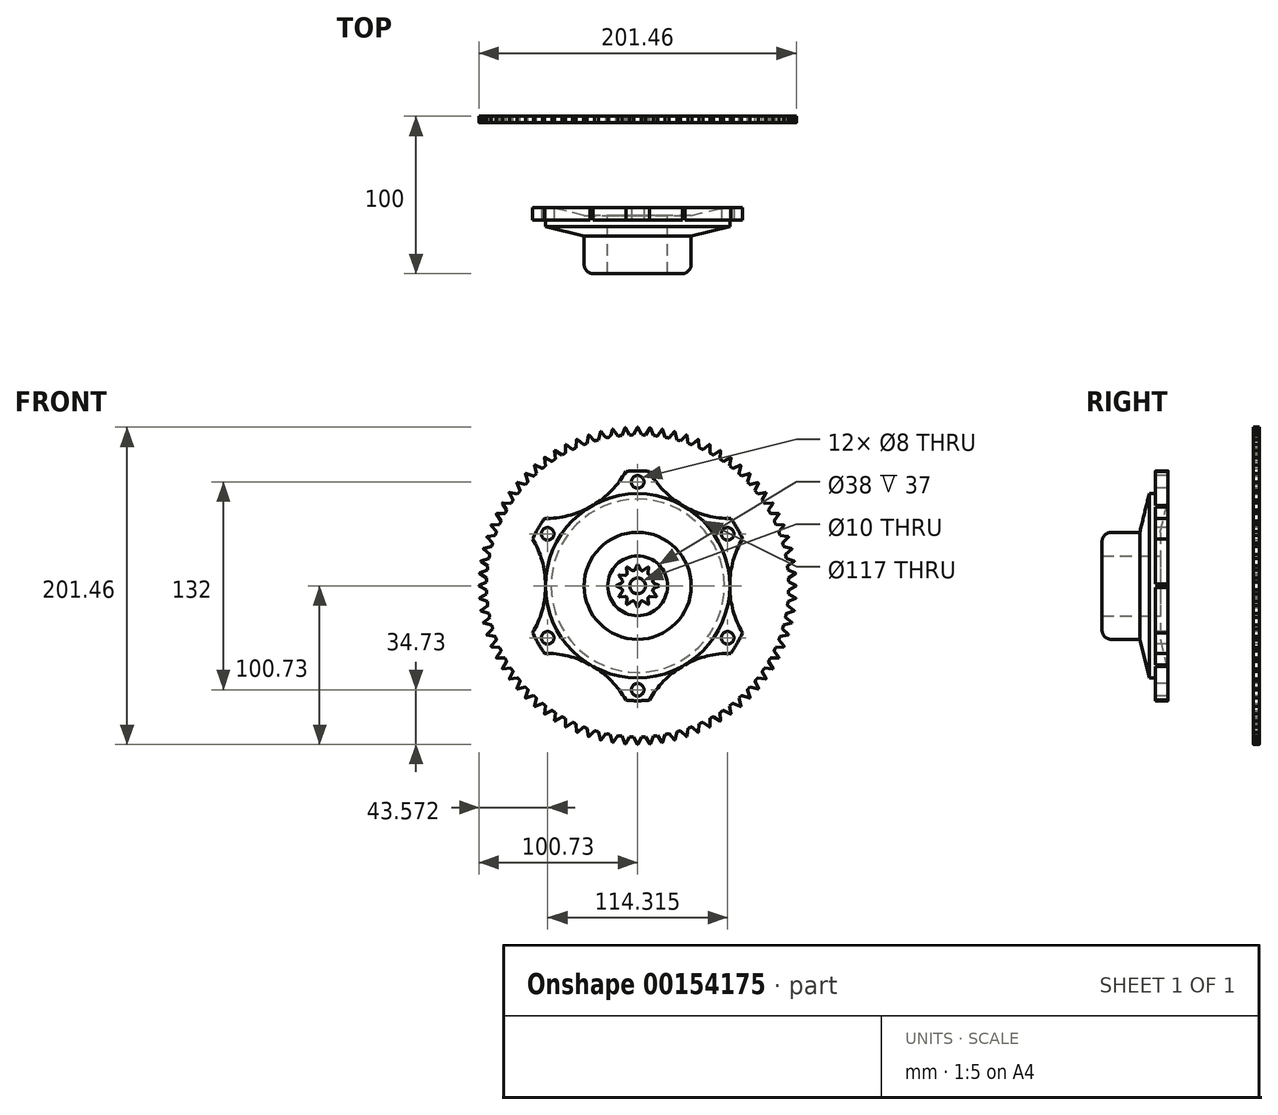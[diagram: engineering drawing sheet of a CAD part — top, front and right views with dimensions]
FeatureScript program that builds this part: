
annotation { "Feature Type Name" : "Feature", "Feature Type Description" : "" }
export const myFeature = defineFeature(function(context is Context, id is Id, definition is map)
    precondition{}
    {
        {
            var Q0;
            Q0=qCreatedBy(makeId("Front.planeOp"),FACE);
            var sketch = newSketch(context, id + "F0", { "sketchPlane" : qUnion([Q0])});
            skCircle(sketch, "E0", {"center": v(0, 0) * mm, "radius": 58.5 * mm});
            skCircle(sketch, "E1", {"center": v(0, 0) * mm, "radius": 96 * mm});
            skPoint(sketch, "E2", {"position": v(0, 101) * mm});
            skPoint(sketch, "E3", {"position": v(0, 96) * mm});
            skPoint(sketch, "E4", {"position": v(-2.5, 95.97) * mm});
            skPoint(sketch, "E5", {"position": v(2.5, 95.97) * mm});
            skLineSegment(sketch, "E6", {"start": v(-0.2, 100.6) * mm, "end": v(-2.5, 95.97) * mm});
            skLineSegment(sketch, "E7", {"start": v(0.2, 100.6) * mm, "end": v(2.5, 95.97) * mm});
            skArc(sketch, "E8.filletArc", {"start": v(0.2, 100.6) * mm, "mid": v(0, 100.73) * mm, "end": v(-0.2, 100.6) * mm});
            skLineSegment(sketch, "E9.1.0", {"start": v(-8.09, 100.28) * mm, "end": v(-10.02, 95.48) * mm});
            skLineSegment(sketch, "E9.1.1", {"start": v(-7.7, 100.3) * mm, "end": v(-5.04, 95.87) * mm});
            skArc(sketch, "E9.1.2", {"start": v(-7.7, 100.3) * mm, "mid": v(-7.9, 100.42) * mm, "end": v(-8.09, 100.28) * mm});
            skLineSegment(sketch, "E9.2.0", {"start": v(-15.93, 99.33) * mm, "end": v(-17.48, 94.4) * mm});
            skLineSegment(sketch, "E9.2.1", {"start": v(-15.54, 99.4) * mm, "end": v(-12.54, 95.18) * mm});
            skArc(sketch, "E9.2.2", {"start": v(-15.54, 99.4) * mm, "mid": v(-15.76, 99.49) * mm, "end": v(-15.93, 99.33) * mm});
            skLineSegment(sketch, "E9.3.0", {"start": v(-23.68, 97.78) * mm, "end": v(-24.83, 92.73) * mm});
            skLineSegment(sketch, "E9.3.1", {"start": v(-23.3, 97.87) * mm, "end": v(-19.97, 93.9) * mm});
            skArc(sketch, "E9.3.2", {"start": v(-23.3, 97.87) * mm, "mid": v(-23.51, 97.94) * mm, "end": v(-23.68, 97.78) * mm});
            skLineSegment(sketch, "E9.4.0", {"start": v(-31.28, 95.62) * mm, "end": v(-32.03, 90.5) * mm});
            skLineSegment(sketch, "E9.4.1", {"start": v(-30.9, 95.74) * mm, "end": v(-27.28, 92.04) * mm});
            skArc(sketch, "E9.4.2", {"start": v(-30.9, 95.74) * mm, "mid": v(-31.13, 95.8) * mm, "end": v(-31.28, 95.62) * mm});
            skLineSegment(sketch, "E9.5.0", {"start": v(-38.68, 92.87) * mm, "end": v(-39.03, 87.7) * mm});
            skLineSegment(sketch, "E9.5.1", {"start": v(-38.32, 93.02) * mm, "end": v(-34.42, 89.62) * mm});
            skArc(sketch, "E9.5.2", {"start": v(-38.32, 93.02) * mm, "mid": v(-38.55, 93.06) * mm, "end": v(-38.68, 92.87) * mm});
            skLineSegment(sketch, "E9.6.0", {"start": v(-45.85, 89.55) * mm, "end": v(-45.8, 84.37) * mm});
            skLineSegment(sketch, "E9.6.1", {"start": v(-45.5, 89.73) * mm, "end": v(-41.34, 86.64) * mm});
            skArc(sketch, "E9.6.2", {"start": v(-45.5, 89.73) * mm, "mid": v(-45.73, 89.75) * mm, "end": v(-45.85, 89.55) * mm});
            skLineSegment(sketch, "E9.7.0", {"start": v(-52.73, 85.68) * mm, "end": v(-52.27, 80.52) * mm});
            skLineSegment(sketch, "E9.7.1", {"start": v(-52.4, 85.88) * mm, "end": v(-48.01, 83.13) * mm});
            skArc(sketch, "E9.7.2", {"start": v(-52.4, 85.88) * mm, "mid": v(-52.63, 85.88) * mm, "end": v(-52.73, 85.68) * mm});
            skLineSegment(sketch, "E9.8.0", {"start": v(-59.3, 81.27) * mm, "end": v(-58.43, 76.17) * mm});
            skLineSegment(sketch, "E9.8.1", {"start": v(-58.97, 81.5) * mm, "end": v(-54.39, 79.1) * mm});
            skArc(sketch, "E9.8.2", {"start": v(-58.97, 81.5) * mm, "mid": v(-59.2, 81.49) * mm, "end": v(-59.3, 81.27) * mm});
            skLineSegment(sketch, "E9.9.0", {"start": v(-65.49, 76.37) * mm, "end": v(-64.23, 71.35) * mm});
            skLineSegment(sketch, "E9.9.1", {"start": v(-65.19, 76.63) * mm, "end": v(-60.42, 74.6) * mm});
            skArc(sketch, "E9.9.2", {"start": v(-65.19, 76.63) * mm, "mid": v(-65.42, 76.6) * mm, "end": v(-65.49, 76.37) * mm});
            skLineSegment(sketch, "E9.10.0", {"start": v(-71.28, 71) * mm, "end": v(-69.63, 66.1) * mm});
            skLineSegment(sketch, "E9.10.1", {"start": v(-71, 71.28) * mm, "end": v(-66.1, 69.63) * mm});
            skArc(sketch, "E9.10.2", {"start": v(-71, 71.28) * mm, "mid": v(-71.22, 71.22) * mm, "end": v(-71.28, 71) * mm});
            skLineSegment(sketch, "E9.11.0", {"start": v(-76.63, 65.19) * mm, "end": v(-74.6, 60.43) * mm});
            skLineSegment(sketch, "E9.11.1", {"start": v(-76.37, 65.49) * mm, "end": v(-71.35, 64.23) * mm});
            skArc(sketch, "E9.11.2", {"start": v(-76.37, 65.49) * mm, "mid": v(-76.6, 65.42) * mm, "end": v(-76.63, 65.19) * mm});
            skLineSegment(sketch, "E9.12.0", {"start": v(-81.5, 58.97) * mm, "end": v(-79.1, 54.39) * mm});
            skLineSegment(sketch, "E9.12.1", {"start": v(-81.27, 59.3) * mm, "end": v(-76.17, 58.43) * mm});
            skArc(sketch, "E9.12.2", {"start": v(-81.27, 59.3) * mm, "mid": v(-81.49, 59.2) * mm, "end": v(-81.5, 58.97) * mm});
            skLineSegment(sketch, "E9.13.0", {"start": v(-85.88, 52.4) * mm, "end": v(-83.13, 48.01) * mm});
            skLineSegment(sketch, "E9.13.1", {"start": v(-85.68, 52.73) * mm, "end": v(-80.52, 52.27) * mm});
            skArc(sketch, "E9.13.2", {"start": v(-85.68, 52.73) * mm, "mid": v(-85.88, 52.63) * mm, "end": v(-85.88, 52.4) * mm});
            skLineSegment(sketch, "E9.14.0", {"start": v(-89.73, 45.5) * mm, "end": v(-86.64, 41.34) * mm});
            skLineSegment(sketch, "E9.14.1", {"start": v(-89.55, 45.85) * mm, "end": v(-84.37, 45.8) * mm});
            skArc(sketch, "E9.14.2", {"start": v(-89.55, 45.85) * mm, "mid": v(-89.75, 45.73) * mm, "end": v(-89.73, 45.5) * mm});
            skLineSegment(sketch, "E9.15.0", {"start": v(-93.02, 38.32) * mm, "end": v(-89.62, 34.42) * mm});
            skLineSegment(sketch, "E9.15.1", {"start": v(-92.87, 38.68) * mm, "end": v(-87.7, 39.03) * mm});
            skArc(sketch, "E9.15.2", {"start": v(-92.87, 38.68) * mm, "mid": v(-93.06, 38.55) * mm, "end": v(-93.02, 38.32) * mm});
            skLineSegment(sketch, "E9.16.0", {"start": v(-95.74, 30.9) * mm, "end": v(-92.04, 27.28) * mm});
            skLineSegment(sketch, "E9.16.1", {"start": v(-95.62, 31.28) * mm, "end": v(-90.5, 32.03) * mm});
            skArc(sketch, "E9.16.2", {"start": v(-95.62, 31.28) * mm, "mid": v(-95.8, 31.13) * mm, "end": v(-95.74, 30.9) * mm});
            skLineSegment(sketch, "E9.17.0", {"start": v(-97.87, 23.3) * mm, "end": v(-93.9, 19.97) * mm});
            skLineSegment(sketch, "E9.17.1", {"start": v(-97.78, 23.68) * mm, "end": v(-92.73, 24.83) * mm});
            skArc(sketch, "E9.17.2", {"start": v(-97.78, 23.68) * mm, "mid": v(-97.94, 23.51) * mm, "end": v(-97.87, 23.3) * mm});
            skLineSegment(sketch, "E9.18.0", {"start": v(-99.4, 15.54) * mm, "end": v(-95.18, 12.54) * mm});
            skLineSegment(sketch, "E9.18.1", {"start": v(-99.33, 15.93) * mm, "end": v(-94.4, 17.48) * mm});
            skArc(sketch, "E9.18.2", {"start": v(-99.33, 15.93) * mm, "mid": v(-99.49, 15.76) * mm, "end": v(-99.4, 15.54) * mm});
            skLineSegment(sketch, "E9.19.0", {"start": v(-100.3, 7.7) * mm, "end": v(-95.87, 5.04) * mm});
            skLineSegment(sketch, "E9.19.1", {"start": v(-100.28, 8.09) * mm, "end": v(-95.48, 10.02) * mm});
            skArc(sketch, "E9.19.2", {"start": v(-100.28, 8.09) * mm, "mid": v(-100.42, 7.9) * mm, "end": v(-100.3, 7.7) * mm});
            skLineSegment(sketch, "E9.20.0", {"start": v(-100.6, -0.2) * mm, "end": v(-95.97, -2.5) * mm});
            skLineSegment(sketch, "E9.20.1", {"start": v(-100.6, 0.2) * mm, "end": v(-95.97, 2.5) * mm});
            skArc(sketch, "E9.20.2", {"start": v(-100.6, 0.2) * mm, "mid": v(-100.73, 0) * mm, "end": v(-100.6, -0.2) * mm});
            skLineSegment(sketch, "E9.21.0", {"start": v(-100.28, -8.09) * mm, "end": v(-95.48, -10.02) * mm});
            skLineSegment(sketch, "E9.21.1", {"start": v(-100.3, -7.7) * mm, "end": v(-95.87, -5.04) * mm});
            skArc(sketch, "E9.21.2", {"start": v(-100.3, -7.7) * mm, "mid": v(-100.42, -7.9) * mm, "end": v(-100.28, -8.09) * mm});
            skLineSegment(sketch, "E9.22.0", {"start": v(-99.33, -15.93) * mm, "end": v(-94.4, -17.48) * mm});
            skLineSegment(sketch, "E9.22.1", {"start": v(-99.4, -15.54) * mm, "end": v(-95.18, -12.54) * mm});
            skArc(sketch, "E9.22.2", {"start": v(-99.4, -15.54) * mm, "mid": v(-99.49, -15.76) * mm, "end": v(-99.33, -15.93) * mm});
            skLineSegment(sketch, "E9.23.0", {"start": v(-97.78, -23.68) * mm, "end": v(-92.73, -24.83) * mm});
            skLineSegment(sketch, "E9.23.1", {"start": v(-97.87, -23.3) * mm, "end": v(-93.9, -19.97) * mm});
            skArc(sketch, "E9.23.2", {"start": v(-97.87, -23.3) * mm, "mid": v(-97.94, -23.51) * mm, "end": v(-97.78, -23.68) * mm});
            skLineSegment(sketch, "E9.24.0", {"start": v(-95.62, -31.28) * mm, "end": v(-90.5, -32.03) * mm});
            skLineSegment(sketch, "E9.24.1", {"start": v(-95.74, -30.9) * mm, "end": v(-92.04, -27.28) * mm});
            skArc(sketch, "E9.24.2", {"start": v(-95.74, -30.9) * mm, "mid": v(-95.8, -31.13) * mm, "end": v(-95.62, -31.28) * mm});
            skLineSegment(sketch, "E9.25.0", {"start": v(-92.87, -38.68) * mm, "end": v(-87.7, -39.03) * mm});
            skLineSegment(sketch, "E9.25.1", {"start": v(-93.02, -38.32) * mm, "end": v(-89.62, -34.42) * mm});
            skArc(sketch, "E9.25.2", {"start": v(-93.02, -38.32) * mm, "mid": v(-93.06, -38.55) * mm, "end": v(-92.87, -38.68) * mm});
            skLineSegment(sketch, "E9.26.0", {"start": v(-89.55, -45.85) * mm, "end": v(-84.37, -45.8) * mm});
            skLineSegment(sketch, "E9.26.1", {"start": v(-89.73, -45.5) * mm, "end": v(-86.64, -41.34) * mm});
            skArc(sketch, "E9.26.2", {"start": v(-89.73, -45.5) * mm, "mid": v(-89.75, -45.73) * mm, "end": v(-89.55, -45.85) * mm});
            skLineSegment(sketch, "E9.27.0", {"start": v(-85.68, -52.73) * mm, "end": v(-80.52, -52.27) * mm});
            skLineSegment(sketch, "E9.27.1", {"start": v(-85.88, -52.4) * mm, "end": v(-83.13, -48.01) * mm});
            skArc(sketch, "E9.27.2", {"start": v(-85.88, -52.4) * mm, "mid": v(-85.88, -52.63) * mm, "end": v(-85.68, -52.73) * mm});
            skLineSegment(sketch, "E9.28.0", {"start": v(-81.27, -59.3) * mm, "end": v(-76.17, -58.43) * mm});
            skLineSegment(sketch, "E9.28.1", {"start": v(-81.5, -58.97) * mm, "end": v(-79.1, -54.39) * mm});
            skArc(sketch, "E9.28.2", {"start": v(-81.5, -58.97) * mm, "mid": v(-81.49, -59.2) * mm, "end": v(-81.27, -59.3) * mm});
            skLineSegment(sketch, "E9.29.0", {"start": v(-76.37, -65.49) * mm, "end": v(-71.35, -64.23) * mm});
            skLineSegment(sketch, "E9.29.1", {"start": v(-76.63, -65.19) * mm, "end": v(-74.6, -60.42) * mm});
            skArc(sketch, "E9.29.2", {"start": v(-76.63, -65.19) * mm, "mid": v(-76.6, -65.42) * mm, "end": v(-76.37, -65.49) * mm});
            skLineSegment(sketch, "E9.30.0", {"start": v(-71, -71.28) * mm, "end": v(-66.1, -69.63) * mm});
            skLineSegment(sketch, "E9.30.1", {"start": v(-71.28, -71) * mm, "end": v(-69.63, -66.1) * mm});
            skArc(sketch, "E9.30.2", {"start": v(-71.28, -71) * mm, "mid": v(-71.22, -71.22) * mm, "end": v(-71, -71.28) * mm});
            skLineSegment(sketch, "E9.31.0", {"start": v(-65.19, -76.63) * mm, "end": v(-60.43, -74.6) * mm});
            skLineSegment(sketch, "E9.31.1", {"start": v(-65.49, -76.37) * mm, "end": v(-64.23, -71.35) * mm});
            skArc(sketch, "E9.31.2", {"start": v(-65.49, -76.37) * mm, "mid": v(-65.42, -76.6) * mm, "end": v(-65.19, -76.63) * mm});
            skLineSegment(sketch, "E9.32.0", {"start": v(-58.97, -81.5) * mm, "end": v(-54.39, -79.1) * mm});
            skLineSegment(sketch, "E9.32.1", {"start": v(-59.3, -81.27) * mm, "end": v(-58.43, -76.17) * mm});
            skArc(sketch, "E9.32.2", {"start": v(-59.3, -81.27) * mm, "mid": v(-59.2, -81.49) * mm, "end": v(-58.97, -81.5) * mm});
            skLineSegment(sketch, "E9.33.0", {"start": v(-52.4, -85.88) * mm, "end": v(-48.01, -83.13) * mm});
            skLineSegment(sketch, "E9.33.1", {"start": v(-52.73, -85.68) * mm, "end": v(-52.27, -80.52) * mm});
            skArc(sketch, "E9.33.2", {"start": v(-52.73, -85.68) * mm, "mid": v(-52.63, -85.88) * mm, "end": v(-52.4, -85.88) * mm});
            skLineSegment(sketch, "E9.34.0", {"start": v(-45.5, -89.73) * mm, "end": v(-41.34, -86.64) * mm});
            skLineSegment(sketch, "E9.34.1", {"start": v(-45.85, -89.55) * mm, "end": v(-45.8, -84.37) * mm});
            skArc(sketch, "E9.34.2", {"start": v(-45.85, -89.55) * mm, "mid": v(-45.73, -89.75) * mm, "end": v(-45.5, -89.73) * mm});
            skLineSegment(sketch, "E9.35.0", {"start": v(-38.32, -93.02) * mm, "end": v(-34.42, -89.62) * mm});
            skLineSegment(sketch, "E9.35.1", {"start": v(-38.68, -92.87) * mm, "end": v(-39.03, -87.7) * mm});
            skArc(sketch, "E9.35.2", {"start": v(-38.68, -92.87) * mm, "mid": v(-38.55, -93.06) * mm, "end": v(-38.32, -93.02) * mm});
            skLineSegment(sketch, "E9.36.0", {"start": v(-30.9, -95.74) * mm, "end": v(-27.28, -92.04) * mm});
            skLineSegment(sketch, "E9.36.1", {"start": v(-31.28, -95.62) * mm, "end": v(-32.03, -90.5) * mm});
            skArc(sketch, "E9.36.2", {"start": v(-31.28, -95.62) * mm, "mid": v(-31.13, -95.8) * mm, "end": v(-30.9, -95.74) * mm});
            skLineSegment(sketch, "E9.37.0", {"start": v(-23.3, -97.87) * mm, "end": v(-19.97, -93.9) * mm});
            skLineSegment(sketch, "E9.37.1", {"start": v(-23.68, -97.78) * mm, "end": v(-24.83, -92.73) * mm});
            skArc(sketch, "E9.37.2", {"start": v(-23.68, -97.78) * mm, "mid": v(-23.51, -97.94) * mm, "end": v(-23.3, -97.87) * mm});
            skLineSegment(sketch, "E9.38.0", {"start": v(-15.54, -99.4) * mm, "end": v(-12.54, -95.18) * mm});
            skLineSegment(sketch, "E9.38.1", {"start": v(-15.93, -99.33) * mm, "end": v(-17.48, -94.4) * mm});
            skArc(sketch, "E9.38.2", {"start": v(-15.93, -99.33) * mm, "mid": v(-15.76, -99.49) * mm, "end": v(-15.54, -99.4) * mm});
            skLineSegment(sketch, "E9.39.0", {"start": v(-7.7, -100.3) * mm, "end": v(-5.04, -95.87) * mm});
            skLineSegment(sketch, "E9.39.1", {"start": v(-8.09, -100.28) * mm, "end": v(-10.02, -95.48) * mm});
            skArc(sketch, "E9.39.2", {"start": v(-8.09, -100.28) * mm, "mid": v(-7.9, -100.42) * mm, "end": v(-7.7, -100.3) * mm});
            skLineSegment(sketch, "E9.40.0", {"start": v(0.2, -100.6) * mm, "end": v(2.5, -95.97) * mm});
            skLineSegment(sketch, "E9.40.1", {"start": v(-0.2, -100.6) * mm, "end": v(-2.5, -95.97) * mm});
            skArc(sketch, "E9.40.2", {"start": v(-0.2, -100.6) * mm, "mid": v(0, -100.73) * mm, "end": v(0.2, -100.6) * mm});
            skLineSegment(sketch, "E9.41.0", {"start": v(8.09, -100.28) * mm, "end": v(10.02, -95.48) * mm});
            skLineSegment(sketch, "E9.41.1", {"start": v(7.7, -100.3) * mm, "end": v(5.04, -95.87) * mm});
            skArc(sketch, "E9.41.2", {"start": v(7.7, -100.3) * mm, "mid": v(7.9, -100.42) * mm, "end": v(8.09, -100.28) * mm});
            skLineSegment(sketch, "E9.42.0", {"start": v(15.93, -99.33) * mm, "end": v(17.48, -94.4) * mm});
            skLineSegment(sketch, "E9.42.1", {"start": v(15.54, -99.4) * mm, "end": v(12.54, -95.18) * mm});
            skArc(sketch, "E9.42.2", {"start": v(15.54, -99.4) * mm, "mid": v(15.76, -99.49) * mm, "end": v(15.93, -99.33) * mm});
            skLineSegment(sketch, "E9.43.0", {"start": v(23.68, -97.78) * mm, "end": v(24.83, -92.73) * mm});
            skLineSegment(sketch, "E9.43.1", {"start": v(23.3, -97.87) * mm, "end": v(19.97, -93.9) * mm});
            skArc(sketch, "E9.43.2", {"start": v(23.3, -97.87) * mm, "mid": v(23.51, -97.94) * mm, "end": v(23.68, -97.78) * mm});
            skLineSegment(sketch, "E9.44.0", {"start": v(31.28, -95.62) * mm, "end": v(32.03, -90.5) * mm});
            skLineSegment(sketch, "E9.44.1", {"start": v(30.9, -95.74) * mm, "end": v(27.28, -92.04) * mm});
            skArc(sketch, "E9.44.2", {"start": v(30.9, -95.74) * mm, "mid": v(31.13, -95.8) * mm, "end": v(31.28, -95.62) * mm});
            skLineSegment(sketch, "E9.45.0", {"start": v(38.68, -92.87) * mm, "end": v(39.03, -87.7) * mm});
            skLineSegment(sketch, "E9.45.1", {"start": v(38.32, -93.02) * mm, "end": v(34.42, -89.62) * mm});
            skArc(sketch, "E9.45.2", {"start": v(38.32, -93.02) * mm, "mid": v(38.55, -93.06) * mm, "end": v(38.68, -92.87) * mm});
            skLineSegment(sketch, "E9.46.0", {"start": v(45.85, -89.55) * mm, "end": v(45.8, -84.37) * mm});
            skLineSegment(sketch, "E9.46.1", {"start": v(45.5, -89.73) * mm, "end": v(41.34, -86.64) * mm});
            skArc(sketch, "E9.46.2", {"start": v(45.5, -89.73) * mm, "mid": v(45.73, -89.75) * mm, "end": v(45.85, -89.55) * mm});
            skLineSegment(sketch, "E9.47.0", {"start": v(52.73, -85.68) * mm, "end": v(52.27, -80.52) * mm});
            skLineSegment(sketch, "E9.47.1", {"start": v(52.4, -85.88) * mm, "end": v(48.01, -83.13) * mm});
            skArc(sketch, "E9.47.2", {"start": v(52.4, -85.88) * mm, "mid": v(52.63, -85.88) * mm, "end": v(52.73, -85.68) * mm});
            skLineSegment(sketch, "E9.48.0", {"start": v(59.3, -81.27) * mm, "end": v(58.43, -76.17) * mm});
            skLineSegment(sketch, "E9.48.1", {"start": v(58.97, -81.5) * mm, "end": v(54.39, -79.1) * mm});
            skArc(sketch, "E9.48.2", {"start": v(58.97, -81.5) * mm, "mid": v(59.2, -81.49) * mm, "end": v(59.3, -81.27) * mm});
            skLineSegment(sketch, "E9.49.0", {"start": v(65.49, -76.37) * mm, "end": v(64.23, -71.35) * mm});
            skLineSegment(sketch, "E9.49.1", {"start": v(65.19, -76.63) * mm, "end": v(60.42, -74.6) * mm});
            skArc(sketch, "E9.49.2", {"start": v(65.19, -76.63) * mm, "mid": v(65.42, -76.6) * mm, "end": v(65.49, -76.37) * mm});
            skLineSegment(sketch, "E9.50.0", {"start": v(71.28, -71) * mm, "end": v(69.63, -66.1) * mm});
            skLineSegment(sketch, "E9.50.1", {"start": v(71, -71.28) * mm, "end": v(66.1, -69.63) * mm});
            skArc(sketch, "E9.50.2", {"start": v(71, -71.28) * mm, "mid": v(71.22, -71.22) * mm, "end": v(71.28, -71) * mm});
            skLineSegment(sketch, "E9.51.0", {"start": v(76.63, -65.19) * mm, "end": v(74.6, -60.43) * mm});
            skLineSegment(sketch, "E9.51.1", {"start": v(76.37, -65.49) * mm, "end": v(71.35, -64.23) * mm});
            skArc(sketch, "E9.51.2", {"start": v(76.37, -65.49) * mm, "mid": v(76.6, -65.42) * mm, "end": v(76.63, -65.19) * mm});
            skLineSegment(sketch, "E9.52.0", {"start": v(81.5, -58.97) * mm, "end": v(79.1, -54.39) * mm});
            skLineSegment(sketch, "E9.52.1", {"start": v(81.27, -59.3) * mm, "end": v(76.17, -58.43) * mm});
            skArc(sketch, "E9.52.2", {"start": v(81.27, -59.3) * mm, "mid": v(81.49, -59.2) * mm, "end": v(81.5, -58.97) * mm});
            skLineSegment(sketch, "E9.53.0", {"start": v(85.88, -52.4) * mm, "end": v(83.13, -48.01) * mm});
            skLineSegment(sketch, "E9.53.1", {"start": v(85.68, -52.73) * mm, "end": v(80.52, -52.27) * mm});
            skArc(sketch, "E9.53.2", {"start": v(85.68, -52.73) * mm, "mid": v(85.88, -52.63) * mm, "end": v(85.88, -52.4) * mm});
            skLineSegment(sketch, "E9.54.0", {"start": v(89.73, -45.5) * mm, "end": v(86.64, -41.34) * mm});
            skLineSegment(sketch, "E9.54.1", {"start": v(89.55, -45.85) * mm, "end": v(84.37, -45.8) * mm});
            skArc(sketch, "E9.54.2", {"start": v(89.55, -45.85) * mm, "mid": v(89.75, -45.73) * mm, "end": v(89.73, -45.5) * mm});
            skLineSegment(sketch, "E9.55.0", {"start": v(93.02, -38.32) * mm, "end": v(89.62, -34.42) * mm});
            skLineSegment(sketch, "E9.55.1", {"start": v(92.87, -38.68) * mm, "end": v(87.7, -39.03) * mm});
            skArc(sketch, "E9.55.2", {"start": v(92.87, -38.68) * mm, "mid": v(93.06, -38.55) * mm, "end": v(93.02, -38.32) * mm});
            skLineSegment(sketch, "E9.56.0", {"start": v(95.74, -30.9) * mm, "end": v(92.04, -27.28) * mm});
            skLineSegment(sketch, "E9.56.1", {"start": v(95.62, -31.28) * mm, "end": v(90.5, -32.03) * mm});
            skArc(sketch, "E9.56.2", {"start": v(95.62, -31.28) * mm, "mid": v(95.8, -31.13) * mm, "end": v(95.74, -30.9) * mm});
            skLineSegment(sketch, "E9.57.0", {"start": v(97.87, -23.3) * mm, "end": v(93.9, -19.97) * mm});
            skLineSegment(sketch, "E9.57.1", {"start": v(97.78, -23.68) * mm, "end": v(92.73, -24.83) * mm});
            skArc(sketch, "E9.57.2", {"start": v(97.78, -23.68) * mm, "mid": v(97.94, -23.51) * mm, "end": v(97.87, -23.3) * mm});
            skLineSegment(sketch, "E9.58.0", {"start": v(99.4, -15.54) * mm, "end": v(95.18, -12.54) * mm});
            skLineSegment(sketch, "E9.58.1", {"start": v(99.33, -15.93) * mm, "end": v(94.4, -17.48) * mm});
            skArc(sketch, "E9.58.2", {"start": v(99.33, -15.93) * mm, "mid": v(99.49, -15.76) * mm, "end": v(99.4, -15.54) * mm});
            skLineSegment(sketch, "E9.59.0", {"start": v(100.3, -7.7) * mm, "end": v(95.87, -5.04) * mm});
            skLineSegment(sketch, "E9.59.1", {"start": v(100.28, -8.09) * mm, "end": v(95.48, -10.02) * mm});
            skArc(sketch, "E9.59.2", {"start": v(100.28, -8.09) * mm, "mid": v(100.42, -7.9) * mm, "end": v(100.3, -7.7) * mm});
            skLineSegment(sketch, "E9.60.0", {"start": v(100.6, 0.2) * mm, "end": v(95.97, 2.5) * mm});
            skLineSegment(sketch, "E9.60.1", {"start": v(100.6, -0.2) * mm, "end": v(95.97, -2.5) * mm});
            skArc(sketch, "E9.60.2", {"start": v(100.6, -0.2) * mm, "mid": v(100.73, 0) * mm, "end": v(100.6, 0.2) * mm});
            skLineSegment(sketch, "E9.61.0", {"start": v(100.28, 8.09) * mm, "end": v(95.48, 10.02) * mm});
            skLineSegment(sketch, "E9.61.1", {"start": v(100.3, 7.7) * mm, "end": v(95.87, 5.04) * mm});
            skArc(sketch, "E9.61.2", {"start": v(100.3, 7.7) * mm, "mid": v(100.42, 7.9) * mm, "end": v(100.28, 8.09) * mm});
            skLineSegment(sketch, "E9.62.0", {"start": v(99.33, 15.93) * mm, "end": v(94.4, 17.48) * mm});
            skLineSegment(sketch, "E9.62.1", {"start": v(99.4, 15.54) * mm, "end": v(95.18, 12.54) * mm});
            skArc(sketch, "E9.62.2", {"start": v(99.4, 15.54) * mm, "mid": v(99.49, 15.76) * mm, "end": v(99.33, 15.93) * mm});
            skLineSegment(sketch, "E9.63.0", {"start": v(97.78, 23.68) * mm, "end": v(92.73, 24.83) * mm});
            skLineSegment(sketch, "E9.63.1", {"start": v(97.87, 23.3) * mm, "end": v(93.9, 19.97) * mm});
            skArc(sketch, "E9.63.2", {"start": v(97.87, 23.3) * mm, "mid": v(97.94, 23.51) * mm, "end": v(97.78, 23.68) * mm});
            skLineSegment(sketch, "E9.64.0", {"start": v(95.62, 31.28) * mm, "end": v(90.5, 32.03) * mm});
            skLineSegment(sketch, "E9.64.1", {"start": v(95.74, 30.9) * mm, "end": v(92.04, 27.28) * mm});
            skArc(sketch, "E9.64.2", {"start": v(95.74, 30.9) * mm, "mid": v(95.8, 31.13) * mm, "end": v(95.62, 31.28) * mm});
            skLineSegment(sketch, "E9.65.0", {"start": v(92.87, 38.68) * mm, "end": v(87.7, 39.03) * mm});
            skLineSegment(sketch, "E9.65.1", {"start": v(93.02, 38.32) * mm, "end": v(89.62, 34.42) * mm});
            skArc(sketch, "E9.65.2", {"start": v(93.02, 38.32) * mm, "mid": v(93.06, 38.55) * mm, "end": v(92.87, 38.68) * mm});
            skLineSegment(sketch, "E9.66.0", {"start": v(89.55, 45.85) * mm, "end": v(84.37, 45.8) * mm});
            skLineSegment(sketch, "E9.66.1", {"start": v(89.73, 45.5) * mm, "end": v(86.64, 41.34) * mm});
            skArc(sketch, "E9.66.2", {"start": v(89.73, 45.5) * mm, "mid": v(89.75, 45.73) * mm, "end": v(89.55, 45.85) * mm});
            skLineSegment(sketch, "E9.67.0", {"start": v(85.68, 52.73) * mm, "end": v(80.52, 52.27) * mm});
            skLineSegment(sketch, "E9.67.1", {"start": v(85.88, 52.4) * mm, "end": v(83.13, 48.01) * mm});
            skArc(sketch, "E9.67.2", {"start": v(85.88, 52.4) * mm, "mid": v(85.88, 52.63) * mm, "end": v(85.68, 52.73) * mm});
            skLineSegment(sketch, "E9.68.0", {"start": v(81.27, 59.3) * mm, "end": v(76.17, 58.43) * mm});
            skLineSegment(sketch, "E9.68.1", {"start": v(81.5, 58.97) * mm, "end": v(79.1, 54.39) * mm});
            skArc(sketch, "E9.68.2", {"start": v(81.5, 58.97) * mm, "mid": v(81.49, 59.2) * mm, "end": v(81.27, 59.3) * mm});
            skLineSegment(sketch, "E9.69.0", {"start": v(76.37, 65.49) * mm, "end": v(71.35, 64.23) * mm});
            skLineSegment(sketch, "E9.69.1", {"start": v(76.63, 65.19) * mm, "end": v(74.6, 60.42) * mm});
            skArc(sketch, "E9.69.2", {"start": v(76.63, 65.19) * mm, "mid": v(76.6, 65.42) * mm, "end": v(76.37, 65.49) * mm});
            skLineSegment(sketch, "E9.70.0", {"start": v(71, 71.28) * mm, "end": v(66.1, 69.63) * mm});
            skLineSegment(sketch, "E9.70.1", {"start": v(71.28, 71) * mm, "end": v(69.63, 66.1) * mm});
            skArc(sketch, "E9.70.2", {"start": v(71.28, 71) * mm, "mid": v(71.22, 71.22) * mm, "end": v(71, 71.28) * mm});
            skLineSegment(sketch, "E9.71.0", {"start": v(65.19, 76.63) * mm, "end": v(60.43, 74.6) * mm});
            skLineSegment(sketch, "E9.71.1", {"start": v(65.49, 76.37) * mm, "end": v(64.23, 71.35) * mm});
            skArc(sketch, "E9.71.2", {"start": v(65.49, 76.37) * mm, "mid": v(65.42, 76.6) * mm, "end": v(65.19, 76.63) * mm});
            skLineSegment(sketch, "E9.72.0", {"start": v(58.97, 81.5) * mm, "end": v(54.39, 79.1) * mm});
            skLineSegment(sketch, "E9.72.1", {"start": v(59.3, 81.27) * mm, "end": v(58.43, 76.17) * mm});
            skArc(sketch, "E9.72.2", {"start": v(59.3, 81.27) * mm, "mid": v(59.2, 81.49) * mm, "end": v(58.97, 81.5) * mm});
            skLineSegment(sketch, "E9.73.0", {"start": v(52.4, 85.88) * mm, "end": v(48.01, 83.13) * mm});
            skLineSegment(sketch, "E9.73.1", {"start": v(52.73, 85.68) * mm, "end": v(52.27, 80.52) * mm});
            skArc(sketch, "E9.73.2", {"start": v(52.73, 85.68) * mm, "mid": v(52.63, 85.88) * mm, "end": v(52.4, 85.88) * mm});
            skLineSegment(sketch, "E9.74.0", {"start": v(45.5, 89.73) * mm, "end": v(41.34, 86.64) * mm});
            skLineSegment(sketch, "E9.74.1", {"start": v(45.85, 89.55) * mm, "end": v(45.8, 84.37) * mm});
            skArc(sketch, "E9.74.2", {"start": v(45.85, 89.55) * mm, "mid": v(45.73, 89.75) * mm, "end": v(45.5, 89.73) * mm});
            skLineSegment(sketch, "E9.75.0", {"start": v(38.32, 93.02) * mm, "end": v(34.42, 89.62) * mm});
            skLineSegment(sketch, "E9.75.1", {"start": v(38.68, 92.87) * mm, "end": v(39.03, 87.7) * mm});
            skArc(sketch, "E9.75.2", {"start": v(38.68, 92.87) * mm, "mid": v(38.55, 93.06) * mm, "end": v(38.32, 93.02) * mm});
            skLineSegment(sketch, "E9.76.0", {"start": v(30.9, 95.74) * mm, "end": v(27.28, 92.04) * mm});
            skLineSegment(sketch, "E9.76.1", {"start": v(31.28, 95.62) * mm, "end": v(32.03, 90.5) * mm});
            skArc(sketch, "E9.76.2", {"start": v(31.28, 95.62) * mm, "mid": v(31.13, 95.8) * mm, "end": v(30.9, 95.74) * mm});
            skLineSegment(sketch, "E9.77.0", {"start": v(23.3, 97.87) * mm, "end": v(19.97, 93.9) * mm});
            skLineSegment(sketch, "E9.77.1", {"start": v(23.68, 97.78) * mm, "end": v(24.83, 92.73) * mm});
            skArc(sketch, "E9.77.2", {"start": v(23.68, 97.78) * mm, "mid": v(23.51, 97.94) * mm, "end": v(23.3, 97.87) * mm});
            skLineSegment(sketch, "E9.78.0", {"start": v(15.54, 99.4) * mm, "end": v(12.54, 95.18) * mm});
            skLineSegment(sketch, "E9.78.1", {"start": v(15.93, 99.33) * mm, "end": v(17.48, 94.4) * mm});
            skArc(sketch, "E9.78.2", {"start": v(15.93, 99.33) * mm, "mid": v(15.76, 99.49) * mm, "end": v(15.54, 99.4) * mm});
            skLineSegment(sketch, "E9.79.0", {"start": v(7.7, 100.3) * mm, "end": v(5.04, 95.87) * mm});
            skLineSegment(sketch, "E9.79.1", {"start": v(8.09, 100.28) * mm, "end": v(10.02, 95.48) * mm});
            skArc(sketch, "E9.79.2", {"start": v(8.09, 100.28) * mm, "mid": v(7.9, 100.42) * mm, "end": v(7.7, 100.3) * mm});
            skSolve(sketch);
        }
        {
            var Q0;
            Q0=qSketchRegion(id+"F0",true);
            extrude(context, id + "F1", {"entities" : qUnion([Q0]), "depth" : 4 * mm, "offsetDistance" : 25 * mm});
        }
        {
            var Q0;
            Q0=makeQuery(id+"F1.opExtrude","SWEPT_EDGE",EDGE,{"disambiguationData":[OSD([sQuery(id+"F0.wireOp",EDGE,"E1"),sQuery(id+"F0.wireOp",EDGE,"E9.3.1")])]});
            var Q1;
            Q1=makeQuery(id+"F1.opExtrude","SWEPT_EDGE",EDGE,{"disambiguationData":[OSD([sQuery(id+"F0.wireOp",EDGE,"E1"),sQuery(id+"F0.wireOp",EDGE,"E9.2.0")])]});
            fillet(context, id + "F2", {"entities" : qUnion([Q0, Q1]), "radius" : 2.5 * mm, "tangentPropagation" : true, "allowEdgeOverflow" : false});
        }
        {
            var Q0;
            Q0=qCreatedBy(makeId("Front.planeOp"),FACE);
            var sketch = newSketch(context, id + "F3", { "sketchPlane" : qUnion([Q0])});
            skCircle(sketch, "E10", {"center": v(0, 0) * mm, "radius": 10 * mm});
            skCircle(sketch, "E11", {"center": v(0, 0) * mm, "radius": 5 * mm});
            skPoint(sketch, "E12", {"position": v(0, 14) * mm});
            skPoint(sketch, "E13", {"position": v(-2, 9.8) * mm});
            skPoint(sketch, "E14", {"position": v(2, 9.8) * mm});
            skLineSegment(sketch, "E15", {"start": v(-0.23, 13.53) * mm, "end": v(-2, 9.8) * mm});
            skLineSegment(sketch, "E16", {"start": v(0.23, 13.53) * mm, "end": v(2, 9.8) * mm});
            skArc(sketch, "E17.filletArc", {"start": v(0.23, 13.53) * mm, "mid": v(0, 13.67) * mm, "end": v(-0.23, 13.53) * mm});
            skPoint(sketch, "E18", {"position": v(1.76, 10.3) * mm});
            skPoint(sketch, "E19", {"position": v(2.5, 9.68) * mm});
            skArc(sketch, "E20", {"start": v(1.76, 10.3) * mm, "mid": v(2.05, 9.9) * mm, "end": v(2.5, 9.68) * mm});
            skArc(sketch, "E21.MirrorCS", {"start": v(-1.76, 10.3) * mm, "mid": v(-2.05, 9.9) * mm, "end": v(-2.5, 9.68) * mm});
            skLineSegment(sketch, "E22.1.0", {"start": v(-6.57, 11.83) * mm, "end": v(-3.17, 9.49) * mm});
            skLineSegment(sketch, "E22.1.1", {"start": v(-6.96, 11.6) * mm, "end": v(-6.63, 7.49) * mm});
            skArc(sketch, "E22.1.2", {"start": v(-6.67, 8.04) * mm, "mid": v(-6.73, 7.54) * mm, "end": v(-7, 7.14) * mm});
            skArc(sketch, "E22.1.3", {"start": v(-6.57, 11.83) * mm, "mid": v(-6.83, 11.84) * mm, "end": v(-6.96, 11.6) * mm});
            skArc(sketch, "E22.1.4", {"start": v(-3.62, 9.8) * mm, "mid": v(-3.17, 9.6) * mm, "end": v(-2.68, 9.64) * mm});
            skLineSegment(sketch, "E22.2.0", {"start": v(-11.6, 6.96) * mm, "end": v(-7.49, 6.63) * mm});
            skLineSegment(sketch, "E22.2.1", {"start": v(-11.83, 6.57) * mm, "end": v(-9.49, 3.17) * mm});
            skArc(sketch, "E22.2.2", {"start": v(-9.8, 3.62) * mm, "mid": v(-9.6, 3.17) * mm, "end": v(-9.64, 2.68) * mm});
            skArc(sketch, "E22.2.3", {"start": v(-11.6, 6.96) * mm, "mid": v(-11.84, 6.83) * mm, "end": v(-11.83, 6.57) * mm});
            skArc(sketch, "E22.2.4", {"start": v(-8.04, 6.67) * mm, "mid": v(-7.54, 6.73) * mm, "end": v(-7.14, 7) * mm});
            skLineSegment(sketch, "E22.3.0", {"start": v(-13.53, 0.23) * mm, "end": v(-9.8, 2) * mm});
            skLineSegment(sketch, "E22.3.1", {"start": v(-13.53, -0.23) * mm, "end": v(-9.8, -2) * mm});
            skArc(sketch, "E22.3.2", {"start": v(-10.3, -1.76) * mm, "mid": v(-9.9, -2.05) * mm, "end": v(-9.68, -2.5) * mm});
            skArc(sketch, "E22.3.3", {"start": v(-13.53, 0.23) * mm, "mid": v(-13.67, 0) * mm, "end": v(-13.53, -0.23) * mm});
            skArc(sketch, "E22.3.4", {"start": v(-10.3, 1.76) * mm, "mid": v(-9.9, 2.05) * mm, "end": v(-9.68, 2.5) * mm});
            skLineSegment(sketch, "E22.4.0", {"start": v(-11.83, -6.57) * mm, "end": v(-9.49, -3.17) * mm});
            skLineSegment(sketch, "E22.4.1", {"start": v(-11.6, -6.96) * mm, "end": v(-7.49, -6.63) * mm});
            skArc(sketch, "E22.4.2", {"start": v(-8.04, -6.67) * mm, "mid": v(-7.54, -6.73) * mm, "end": v(-7.14, -7) * mm});
            skArc(sketch, "E22.4.3", {"start": v(-11.83, -6.57) * mm, "mid": v(-11.84, -6.83) * mm, "end": v(-11.6, -6.96) * mm});
            skArc(sketch, "E22.4.4", {"start": v(-9.8, -3.62) * mm, "mid": v(-9.6, -3.17) * mm, "end": v(-9.64, -2.68) * mm});
            skLineSegment(sketch, "E22.5.0", {"start": v(-6.96, -11.6) * mm, "end": v(-6.63, -7.49) * mm});
            skLineSegment(sketch, "E22.5.1", {"start": v(-6.57, -11.83) * mm, "end": v(-3.17, -9.49) * mm});
            skArc(sketch, "E22.5.2", {"start": v(-3.62, -9.8) * mm, "mid": v(-3.17, -9.6) * mm, "end": v(-2.68, -9.64) * mm});
            skArc(sketch, "E22.5.3", {"start": v(-6.96, -11.6) * mm, "mid": v(-6.83, -11.84) * mm, "end": v(-6.57, -11.83) * mm});
            skArc(sketch, "E22.5.4", {"start": v(-6.67, -8.04) * mm, "mid": v(-6.73, -7.54) * mm, "end": v(-7, -7.14) * mm});
            skLineSegment(sketch, "E22.6.0", {"start": v(-0.23, -13.53) * mm, "end": v(-2, -9.8) * mm});
            skLineSegment(sketch, "E22.6.1", {"start": v(0.23, -13.53) * mm, "end": v(2, -9.8) * mm});
            skArc(sketch, "E22.6.2", {"start": v(1.76, -10.3) * mm, "mid": v(2.05, -9.9) * mm, "end": v(2.5, -9.68) * mm});
            skArc(sketch, "E22.6.3", {"start": v(-0.23, -13.53) * mm, "mid": v(0, -13.67) * mm, "end": v(0.23, -13.53) * mm});
            skArc(sketch, "E22.6.4", {"start": v(-1.76, -10.3) * mm, "mid": v(-2.05, -9.9) * mm, "end": v(-2.5, -9.68) * mm});
            skLineSegment(sketch, "E22.7.0", {"start": v(6.57, -11.83) * mm, "end": v(3.17, -9.49) * mm});
            skLineSegment(sketch, "E22.7.1", {"start": v(6.96, -11.6) * mm, "end": v(6.63, -7.49) * mm});
            skArc(sketch, "E22.7.2", {"start": v(6.67, -8.04) * mm, "mid": v(6.73, -7.54) * mm, "end": v(7, -7.14) * mm});
            skArc(sketch, "E22.7.3", {"start": v(6.57, -11.83) * mm, "mid": v(6.83, -11.84) * mm, "end": v(6.96, -11.6) * mm});
            skArc(sketch, "E22.7.4", {"start": v(3.62, -9.8) * mm, "mid": v(3.17, -9.6) * mm, "end": v(2.68, -9.64) * mm});
            skLineSegment(sketch, "E22.8.0", {"start": v(11.6, -6.96) * mm, "end": v(7.49, -6.63) * mm});
            skLineSegment(sketch, "E22.8.1", {"start": v(11.83, -6.57) * mm, "end": v(9.49, -3.17) * mm});
            skArc(sketch, "E22.8.2", {"start": v(9.8, -3.62) * mm, "mid": v(9.6, -3.17) * mm, "end": v(9.64, -2.68) * mm});
            skArc(sketch, "E22.8.3", {"start": v(11.6, -6.96) * mm, "mid": v(11.84, -6.83) * mm, "end": v(11.83, -6.57) * mm});
            skArc(sketch, "E22.8.4", {"start": v(8.04, -6.67) * mm, "mid": v(7.54, -6.73) * mm, "end": v(7.14, -7) * mm});
            skLineSegment(sketch, "E22.9.0", {"start": v(13.53, -0.23) * mm, "end": v(9.8, -2) * mm});
            skLineSegment(sketch, "E22.9.1", {"start": v(13.53, 0.23) * mm, "end": v(9.8, 2) * mm});
            skArc(sketch, "E22.9.2", {"start": v(10.3, 1.76) * mm, "mid": v(9.9, 2.05) * mm, "end": v(9.68, 2.5) * mm});
            skArc(sketch, "E22.9.3", {"start": v(13.53, -0.23) * mm, "mid": v(13.67, 0) * mm, "end": v(13.53, 0.23) * mm});
            skArc(sketch, "E22.9.4", {"start": v(10.3, -1.76) * mm, "mid": v(9.9, -2.05) * mm, "end": v(9.68, -2.5) * mm});
            skLineSegment(sketch, "E22.10.0", {"start": v(11.83, 6.57) * mm, "end": v(9.49, 3.17) * mm});
            skLineSegment(sketch, "E22.10.1", {"start": v(11.6, 6.96) * mm, "end": v(7.49, 6.63) * mm});
            skArc(sketch, "E22.10.2", {"start": v(8.04, 6.67) * mm, "mid": v(7.54, 6.73) * mm, "end": v(7.14, 7) * mm});
            skArc(sketch, "E22.10.3", {"start": v(11.83, 6.57) * mm, "mid": v(11.84, 6.83) * mm, "end": v(11.6, 6.96) * mm});
            skArc(sketch, "E22.10.4", {"start": v(9.8, 3.62) * mm, "mid": v(9.6, 3.17) * mm, "end": v(9.64, 2.68) * mm});
            skLineSegment(sketch, "E22.11.0", {"start": v(6.96, 11.6) * mm, "end": v(6.63, 7.49) * mm});
            skLineSegment(sketch, "E22.11.1", {"start": v(6.57, 11.83) * mm, "end": v(3.17, 9.49) * mm});
            skArc(sketch, "E22.11.2", {"start": v(3.62, 9.8) * mm, "mid": v(3.17, 9.6) * mm, "end": v(2.68, 9.64) * mm});
            skArc(sketch, "E22.11.3", {"start": v(6.96, 11.6) * mm, "mid": v(6.83, 11.84) * mm, "end": v(6.57, 11.83) * mm});
            skArc(sketch, "E22.11.4", {"start": v(6.67, 8.04) * mm, "mid": v(6.73, 7.54) * mm, "end": v(7, 7.14) * mm});
            skSolve(sketch);
        }
        {
            var Q0;
            Q0=qSketchRegion(id+"F3",true);
            extrude(context, id + "F4", {"entities" : qUnion([Q0]), "depth" : 4 * mm, "offsetDistance" : 25 * mm});
        }
        {
            var Q0;
            Q0=qCreatedBy(makeId("Right.planeOp"),FACE);
            var sketch = newSketch(context, id + "F5", { "sketchPlane" : qUnion([Q0])});
            skPoint(sketch, "E23", {"position": v(-100, 0) * mm});
            skLineSegment(sketch, "E24", {"start": v(-100, 0) * mm, "end": v(-100, 34) * mm});
            skLineSegment(sketch, "E25", {"start": v(-100, 34) * mm, "end": v(-63, 34) * mm});
            skLineSegment(sketch, "E26", {"start": v(-63, 34) * mm, "end": v(-63, 0) * mm});
            skLineSegment(sketch, "E27", {"start": v(-63, 0) * mm, "end": v(-100, 0) * mm, "construction": true});
            skPoint(sketch, "E28", {"position": v(-58, 73) * mm});
            skLineSegment(sketch, "E29", {"start": v(-58, 73) * mm, "end": v(-66, 73) * mm});
            skPoint(sketch, "E30", {"position": v(-58, 55) * mm});
            skLineSegment(sketch, "E31", {"start": v(-58, 73) * mm, "end": v(-58, 55) * mm});
            skLineSegment(sketch, "E32", {"start": v(-58, 55) * mm, "end": v(-63, 34) * mm});
            skPoint(sketch, "E33", {"position": v(-66, 58.5) * mm});
            skLineSegment(sketch, "E34", {"start": v(-66, 73) * mm, "end": v(-66, 58.5) * mm});
            skPoint(sketch, "E35", {"position": v(-76, 34) * mm});
            skLineSegment(sketch, "E36", {"start": v(-66, 58.5) * mm, "end": v(-70, 58.5) * mm});
            skLineSegment(sketch, "E37", {"start": v(-70, 58.5) * mm, "end": v(-76, 34) * mm});
            skPoint(sketch, "E38", {"position": v(-100, 19) * mm});
            skLineSegment(sketch, "E39", {"start": v(-100, 19) * mm, "end": v(-63, 19) * mm});
            skSolve(sketch);
        }
        {
            var Q0;
            Q0=qSketchRegion(id+"F5",true);
            var Q1;
            Q1=sQuery(id+"F5.wireOp",EDGE,"E27");
            revolve(context, id + "F6", {"entities" : qUnion([Q0]), "axis" : qUnion([Q1]), "revolveType" : RevolveType.FULL});
        }
        {
            var Q0;
            Q0=makeQuery(id+"F6.opRevolve","SWEPT_FACE",FACE,{"disambiguationData":[OSD([sQuery(id+"F5.wireOp",EDGE,"E34")])]});
            var sketch = newSketch(context, id + "F7", { "sketchPlane" : qUnion([Q0])});
            skPoint(sketch, "E40", {"position": v(0, 66) * mm});
            skCircle(sketch, "E41", {"center": v(0, 66) * mm, "radius": 4 * mm});
            skCircle(sketch, "E42.1.0", {"center": v(-57.16, 33) * mm, "radius": 4 * mm});
            skCircle(sketch, "E42.2.0", {"center": v(-57.16, -33) * mm, "radius": 4 * mm});
            skCircle(sketch, "E42.3.0", {"center": v(0, -66) * mm, "radius": 4 * mm});
            skCircle(sketch, "E42.4.0", {"center": v(57.16, -33) * mm, "radius": 4 * mm});
            skCircle(sketch, "E42.5.0", {"center": v(57.16, 33) * mm, "radius": 4 * mm});
            skPoint(sketch, "E42.center", {"position": v(0, 0) * mm});
            skPoint(sketch, "E43", {"position": v(0, 73) * mm});
            skPoint(sketch, "E44", {"position": v(-7.5, 72.61) * mm});
            skPoint(sketch, "E45", {"position": v(7.5, 72.61) * mm});
            skLineSegment(sketch, "E46", {"start": v(7.5, 72.61) * mm, "end": v(0, 66) * mm});
            skLineSegment(sketch, "E47", {"start": v(-7.5, 72.61) * mm, "end": v(0, 66) * mm});
            skLineSegment(sketch, "E48.1.0", {"start": v(-66.64, 29.81) * mm, "end": v(-57.16, 33) * mm});
            skLineSegment(sketch, "E48.1.1", {"start": v(-59.14, 42.8) * mm, "end": v(-57.16, 33) * mm});
            skLineSegment(sketch, "E48.2.0", {"start": v(-59.14, -42.8) * mm, "end": v(-57.16, -33) * mm});
            skLineSegment(sketch, "E48.2.1", {"start": v(-66.64, -29.81) * mm, "end": v(-57.16, -33) * mm});
            skLineSegment(sketch, "E48.3.0", {"start": v(7.5, -72.61) * mm, "end": v(0, -66) * mm});
            skLineSegment(sketch, "E48.3.1", {"start": v(-7.5, -72.61) * mm, "end": v(0, -66) * mm});
            skLineSegment(sketch, "E48.4.0", {"start": v(66.64, -29.81) * mm, "end": v(57.16, -33) * mm});
            skLineSegment(sketch, "E48.4.1", {"start": v(59.14, -42.8) * mm, "end": v(57.16, -33) * mm});
            skLineSegment(sketch, "E48.5.0", {"start": v(59.14, 42.8) * mm, "end": v(57.16, 33) * mm});
            skLineSegment(sketch, "E48.5.1", {"start": v(66.64, 29.81) * mm, "end": v(57.16, 33) * mm});
            skCircle(sketch, "E49.0", {"center": v(0, 0) * mm, "radius": 58.5 * mm});
            skLineSegment(sketch, "E50", {"start": v(0, 0) * mm, "end": v(-30.13, 50.14) * mm});
            skLineSegment(sketch, "E51", {"start": v(-30.13, 50.14) * mm, "end": v(0, 0) * mm});
            skLineSegment(sketch, "E52", {"start": v(0, 66) * mm, "end": v(0, 0) * mm, "construction": true});
            skArc(sketch, "E53", {"start": v(-59.14, 42.8) * mm, "mid": v(-29.24, 50.65) * mm, "end": v(-7.5, 72.61) * mm});
            skArc(sketch, "E54.1.0", {"start": v(-66.64, -29.81) * mm, "mid": v(-58.48, 0) * mm, "end": v(-66.64, 29.81) * mm});
            skArc(sketch, "E54.2.0", {"start": v(-7.5, -72.61) * mm, "mid": v(-29.24, -50.65) * mm, "end": v(-59.14, -42.8) * mm});
            skArc(sketch, "E54.3.0", {"start": v(59.14, -42.8) * mm, "mid": v(29.24, -50.65) * mm, "end": v(7.5, -72.61) * mm});
            skArc(sketch, "E54.4.0", {"start": v(66.64, 29.81) * mm, "mid": v(58.48, 0) * mm, "end": v(66.64, -29.81) * mm});
            skArc(sketch, "E54.5.0", {"start": v(7.5, 72.61) * mm, "mid": v(29.24, 50.65) * mm, "end": v(59.14, 42.8) * mm});
            skSolve(sketch);
        }
        {
            var Q0;
            {var subQ0=sQuery(id+"F7.wireOp",EDGE,"E54.5.0");var subQ1=sQuery(id+"F7.wireOp",EDGE,"E49.0");var subQ2=makeQuery(id+"F7.imprint","INTERSECT",VERTEX,{"disambiguationData":[OD(0.0)],"derivedFrom":[subQ1,subQ0]});Q0=makeQuery(id+"F7.imprint","IMPRINT",FACE,{"disambiguationData":[TD([[makeQuery(id+"F7.imprint","IMPRINT",EDGE,{"disambiguationData":[TD([[subQ2,1.0]])],"derivedFrom":subQ1}),1.0]])]});}
            var Q1;
            {var subQ0=sQuery(id+"F7.wireOp",EDGE,"E54.4.0");var subQ1=sQuery(id+"F7.wireOp",EDGE,"E49.0");var subQ2=makeQuery(id+"F7.imprint","INTERSECT",VERTEX,{"disambiguationData":[OD(0.0)],"derivedFrom":[subQ1,subQ0]});Q1=makeQuery(id+"F7.imprint","IMPRINT",FACE,{"disambiguationData":[TD([[makeQuery(id+"F7.imprint","IMPRINT",EDGE,{"disambiguationData":[TD([[subQ2,-1.0]])],"derivedFrom":subQ1}),1.0]])]});}
            var Q2;
            {var subQ0=sQuery(id+"F7.wireOp",EDGE,"E54.3.0");var subQ1=sQuery(id+"F7.wireOp",EDGE,"E49.0");var subQ2=makeQuery(id+"F7.imprint","INTERSECT",VERTEX,{"disambiguationData":[OD(0.0)],"derivedFrom":[subQ1,subQ0]});Q2=makeQuery(id+"F7.imprint","IMPRINT",FACE,{"disambiguationData":[TD([[makeQuery(id+"F7.imprint","IMPRINT",EDGE,{"disambiguationData":[TD([[subQ2,-1.0]])],"derivedFrom":subQ1}),1.0]])]});}
            var Q3;
            {var subQ0=sQuery(id+"F7.wireOp",EDGE,"E54.2.0");var subQ1=sQuery(id+"F7.wireOp",EDGE,"E49.0");var subQ2=makeQuery(id+"F7.imprint","INTERSECT",VERTEX,{"disambiguationData":[OD(0.0)],"derivedFrom":[subQ1,subQ0]});Q3=makeQuery(id+"F7.imprint","IMPRINT",FACE,{"disambiguationData":[TD([[makeQuery(id+"F7.imprint","IMPRINT",EDGE,{"disambiguationData":[TD([[subQ2,-1.0]])],"derivedFrom":subQ1}),1.0]])]});}
            var Q4;
            {var subQ0=sQuery(id+"F7.wireOp",EDGE,"E54.1.0");var subQ1=sQuery(id+"F7.wireOp",EDGE,"E49.0");var subQ2=makeQuery(id+"F7.imprint","INTERSECT",VERTEX,{"disambiguationData":[OD(0.0)],"derivedFrom":[subQ1,subQ0]});Q4=makeQuery(id+"F7.imprint","IMPRINT",FACE,{"disambiguationData":[TD([[makeQuery(id+"F7.imprint","IMPRINT",EDGE,{"disambiguationData":[TD([[subQ2,-1.0]])],"derivedFrom":subQ1}),1.0]])]});}
            var Q5;
            {var subQ0=sQuery(id+"F7.wireOp",EDGE,"E53");var subQ1=sQuery(id+"F7.wireOp",EDGE,"E49.0");var subQ2=makeQuery(id+"F7.imprint","INTERSECT",VERTEX,{"disambiguationData":[OD(0.0)],"derivedFrom":[subQ1,subQ0]});Q5=makeQuery(id+"F7.imprint","IMPRINT",FACE,{"disambiguationData":[TD([[makeQuery(id+"F7.imprint","IMPRINT",EDGE,{"disambiguationData":[TD([[subQ2,-1.0]])],"derivedFrom":subQ1}),1.0]])]});}
            var Q6;
            {var subQ0=sQuery(id+"F7.wireOp",EDGE,"E48.1.0");var subQ1=sQuery(id+"F7.wireOp",EDGE,"E42.1.0");var subQ2=makeQuery(id+"F7.imprint","INTERSECT",VERTEX,{"derivedFrom":[subQ1,subQ0]});Q6=makeQuery(id+"F7.imprint","IMPRINT",FACE,{"disambiguationData":[TD([[makeQuery(id+"F7.imprint","IMPRINT",EDGE,{"disambiguationData":[TD([[subQ2,-1.0]])],"derivedFrom":subQ1}),1.0]])]});}
            var Q7;
            {var subQ0=sQuery(id+"F7.wireOp",EDGE,"E48.1.0");var subQ1=sQuery(id+"F7.wireOp",EDGE,"E42.1.0");var subQ2=makeQuery(id+"F7.imprint","INTERSECT",VERTEX,{"derivedFrom":[subQ1,subQ0]});Q7=makeQuery(id+"F7.imprint","IMPRINT",FACE,{"disambiguationData":[TD([[makeQuery(id+"F7.imprint","IMPRINT",EDGE,{"disambiguationData":[TD([[subQ2,1.0]])],"derivedFrom":subQ1}),1.0]])]});}
            var Q8;
            {var subQ0=sQuery(id+"F7.wireOp",EDGE,"E46");var subQ1=sQuery(id+"F7.wireOp",EDGE,"E41");var subQ2=makeQuery(id+"F7.imprint","INTERSECT",VERTEX,{"derivedFrom":[subQ1,subQ0]});Q8=makeQuery(id+"F7.imprint","IMPRINT",FACE,{"disambiguationData":[TD([[makeQuery(id+"F7.imprint","IMPRINT",EDGE,{"disambiguationData":[TD([[subQ2,-1.0]])],"derivedFrom":subQ1}),1.0]])]});}
            var Q9;
            {var subQ0=sQuery(id+"F7.wireOp",EDGE,"E46");var subQ1=sQuery(id+"F7.wireOp",EDGE,"E41");var subQ2=makeQuery(id+"F7.imprint","INTERSECT",VERTEX,{"derivedFrom":[subQ1,subQ0]});Q9=makeQuery(id+"F7.imprint","IMPRINT",FACE,{"disambiguationData":[TD([[makeQuery(id+"F7.imprint","IMPRINT",EDGE,{"disambiguationData":[TD([[subQ2,1.0]])],"derivedFrom":subQ1}),1.0]])]});}
            var Q10;
            {var subQ0=sQuery(id+"F7.wireOp",EDGE,"E48.5.0");var subQ1=sQuery(id+"F7.wireOp",EDGE,"E42.5.0");var subQ2=makeQuery(id+"F7.imprint","INTERSECT",VERTEX,{"derivedFrom":[subQ1,subQ0]});Q10=makeQuery(id+"F7.imprint","IMPRINT",FACE,{"disambiguationData":[TD([[makeQuery(id+"F7.imprint","IMPRINT",EDGE,{"disambiguationData":[TD([[subQ2,1.0]])],"derivedFrom":subQ1}),1.0]])]});}
            var Q11;
            {var subQ0=sQuery(id+"F7.wireOp",EDGE,"E48.5.0");var subQ1=sQuery(id+"F7.wireOp",EDGE,"E42.5.0");var subQ2=makeQuery(id+"F7.imprint","INTERSECT",VERTEX,{"derivedFrom":[subQ1,subQ0]});Q11=makeQuery(id+"F7.imprint","IMPRINT",FACE,{"disambiguationData":[TD([[makeQuery(id+"F7.imprint","IMPRINT",EDGE,{"disambiguationData":[TD([[subQ2,-1.0]])],"derivedFrom":subQ1}),1.0]])]});}
            var Q12;
            {var subQ0=sQuery(id+"F7.wireOp",EDGE,"E48.4.0");var subQ1=sQuery(id+"F7.wireOp",EDGE,"E42.4.0");var subQ2=makeQuery(id+"F7.imprint","INTERSECT",VERTEX,{"derivedFrom":[subQ1,subQ0]});Q12=makeQuery(id+"F7.imprint","IMPRINT",FACE,{"disambiguationData":[TD([[makeQuery(id+"F7.imprint","IMPRINT",EDGE,{"disambiguationData":[TD([[subQ2,-1.0]])],"derivedFrom":subQ1}),1.0]])]});}
            var Q13;
            {var subQ0=sQuery(id+"F7.wireOp",EDGE,"E48.4.0");var subQ1=sQuery(id+"F7.wireOp",EDGE,"E42.4.0");var subQ2=makeQuery(id+"F7.imprint","INTERSECT",VERTEX,{"derivedFrom":[subQ1,subQ0]});Q13=makeQuery(id+"F7.imprint","IMPRINT",FACE,{"disambiguationData":[TD([[makeQuery(id+"F7.imprint","IMPRINT",EDGE,{"disambiguationData":[TD([[subQ2,1.0]])],"derivedFrom":subQ1}),1.0]])]});}
            var Q14;
            {var subQ0=sQuery(id+"F7.wireOp",EDGE,"E48.3.0");var subQ1=sQuery(id+"F7.wireOp",EDGE,"E42.3.0");var subQ2=makeQuery(id+"F7.imprint","INTERSECT",VERTEX,{"derivedFrom":[subQ1,subQ0]});Q14=makeQuery(id+"F7.imprint","IMPRINT",FACE,{"disambiguationData":[TD([[makeQuery(id+"F7.imprint","IMPRINT",EDGE,{"disambiguationData":[TD([[subQ2,-1.0]])],"derivedFrom":subQ1}),1.0]])]});}
            var Q15;
            {var subQ0=sQuery(id+"F7.wireOp",EDGE,"E48.3.0");var subQ1=sQuery(id+"F7.wireOp",EDGE,"E42.3.0");var subQ2=makeQuery(id+"F7.imprint","INTERSECT",VERTEX,{"derivedFrom":[subQ1,subQ0]});Q15=makeQuery(id+"F7.imprint","IMPRINT",FACE,{"disambiguationData":[TD([[makeQuery(id+"F7.imprint","IMPRINT",EDGE,{"disambiguationData":[TD([[subQ2,1.0]])],"derivedFrom":subQ1}),1.0]])]});}
            var Q16;
            {var subQ0=sQuery(id+"F7.wireOp",EDGE,"E48.2.0");var subQ1=sQuery(id+"F7.wireOp",EDGE,"E42.2.0");var subQ2=makeQuery(id+"F7.imprint","INTERSECT",VERTEX,{"derivedFrom":[subQ1,subQ0]});Q16=makeQuery(id+"F7.imprint","IMPRINT",FACE,{"disambiguationData":[TD([[makeQuery(id+"F7.imprint","IMPRINT",EDGE,{"disambiguationData":[TD([[subQ2,-1.0]])],"derivedFrom":subQ1}),1.0]])]});}
            var Q17;
            {var subQ0=sQuery(id+"F7.wireOp",EDGE,"E48.2.0");var subQ1=sQuery(id+"F7.wireOp",EDGE,"E42.2.0");var subQ2=makeQuery(id+"F7.imprint","INTERSECT",VERTEX,{"derivedFrom":[subQ1,subQ0]});Q17=makeQuery(id+"F7.imprint","IMPRINT",FACE,{"disambiguationData":[TD([[makeQuery(id+"F7.imprint","IMPRINT",EDGE,{"disambiguationData":[TD([[subQ2,1.0]])],"derivedFrom":subQ1}),1.0]])]});}
            extrude(context, id + "F8", {"entities" : qUnion([Q0, Q1, Q2, Q3, Q4, Q5, Q6, Q7, Q8, Q9, Q10, Q11, Q12, Q13, Q14, Q15, Q16, Q17]), "operationType" : NewBodyOperationType.REMOVE, "oppositeDirection" : true, "depth" : 8 * mm, "offsetDistance" : 25 * mm});
        }
        {
            var Q0;
            Q0=makeQuery(id+"F6.opRevolve","SWEPT_EDGE",EDGE,{"disambiguationData":[OSD([sQuery(id+"F5.wireOp",EDGE,"E24"),sQuery(id+"F5.wireOp",EDGE,"E25")])]});
            fillet(context, id + "F9", {"entities" : qUnion([Q0]), "radius" : 6 * mm, "tangentPropagation" : true, "allowEdgeOverflow" : false});
        }
        {
            var Q0;
            Q0=makeQuery(id+"F1.opExtrude","CAP_FACE",FACE,{"disambiguationData":[OSD([sQuery(id+"F0.wireOp",EDGE,"E0"),sQuery(id+"F0.wireOp",EDGE,"E1"),sQuery(id+"F0.wireOp",EDGE,"E6"),sQuery(id+"F0.wireOp",EDGE,"E7"),sQuery(id+"F0.wireOp",EDGE,"E8.filletArc"),sQuery(id+"F0.wireOp",EDGE,"E9.1.0"),sQuery(id+"F0.wireOp",EDGE,"E9.1.1"),sQuery(id+"F0.wireOp",EDGE,"E9.1.2"),sQuery(id+"F0.wireOp",EDGE,"E9.2.0"),sQuery(id+"F0.wireOp",EDGE,"E9.2.1"),sQuery(id+"F0.wireOp",EDGE,"E9.2.2"),sQuery(id+"F0.wireOp",EDGE,"E9.3.0"),sQuery(id+"F0.wireOp",EDGE,"E9.3.1"),sQuery(id+"F0.wireOp",EDGE,"E9.3.2"),sQuery(id+"F0.wireOp",EDGE,"E9.4.0"),sQuery(id+"F0.wireOp",EDGE,"E9.4.1"),sQuery(id+"F0.wireOp",EDGE,"E9.4.2"),sQuery(id+"F0.wireOp",EDGE,"E9.5.0"),sQuery(id+"F0.wireOp",EDGE,"E9.5.1"),sQuery(id+"F0.wireOp",EDGE,"E9.5.2"),sQuery(id+"F0.wireOp",EDGE,"E9.6.0"),sQuery(id+"F0.wireOp",EDGE,"E9.6.1"),sQuery(id+"F0.wireOp",EDGE,"E9.6.2"),sQuery(id+"F0.wireOp",EDGE,"E9.7.0"),sQuery(id+"F0.wireOp",EDGE,"E9.7.1"),sQuery(id+"F0.wireOp",EDGE,"E9.7.2"),sQuery(id+"F0.wireOp",EDGE,"E9.8.0"),sQuery(id+"F0.wireOp",EDGE,"E9.8.1"),sQuery(id+"F0.wireOp",EDGE,"E9.8.2"),sQuery(id+"F0.wireOp",EDGE,"E9.9.0"),sQuery(id+"F0.wireOp",EDGE,"E9.9.1"),sQuery(id+"F0.wireOp",EDGE,"E9.9.2"),sQuery(id+"F0.wireOp",EDGE,"E9.10.0"),sQuery(id+"F0.wireOp",EDGE,"E9.10.1"),sQuery(id+"F0.wireOp",EDGE,"E9.10.2"),sQuery(id+"F0.wireOp",EDGE,"E9.11.0"),sQuery(id+"F0.wireOp",EDGE,"E9.11.1"),sQuery(id+"F0.wireOp",EDGE,"E9.11.2"),sQuery(id+"F0.wireOp",EDGE,"E9.12.0"),sQuery(id+"F0.wireOp",EDGE,"E9.12.1"),sQuery(id+"F0.wireOp",EDGE,"E9.12.2"),sQuery(id+"F0.wireOp",EDGE,"E9.13.0"),sQuery(id+"F0.wireOp",EDGE,"E9.13.1"),sQuery(id+"F0.wireOp",EDGE,"E9.13.2"),sQuery(id+"F0.wireOp",EDGE,"E9.14.0"),sQuery(id+"F0.wireOp",EDGE,"E9.14.1"),sQuery(id+"F0.wireOp",EDGE,"E9.14.2"),sQuery(id+"F0.wireOp",EDGE,"E9.15.0"),sQuery(id+"F0.wireOp",EDGE,"E9.15.1"),sQuery(id+"F0.wireOp",EDGE,"E9.15.2"),sQuery(id+"F0.wireOp",EDGE,"E9.16.0"),sQuery(id+"F0.wireOp",EDGE,"E9.16.1"),sQuery(id+"F0.wireOp",EDGE,"E9.16.2"),sQuery(id+"F0.wireOp",EDGE,"E9.17.0"),sQuery(id+"F0.wireOp",EDGE,"E9.17.1"),sQuery(id+"F0.wireOp",EDGE,"E9.17.2"),sQuery(id+"F0.wireOp",EDGE,"E9.18.0"),sQuery(id+"F0.wireOp",EDGE,"E9.18.1"),sQuery(id+"F0.wireOp",EDGE,"E9.18.2"),sQuery(id+"F0.wireOp",EDGE,"E9.19.0"),sQuery(id+"F0.wireOp",EDGE,"E9.19.1"),sQuery(id+"F0.wireOp",EDGE,"E9.19.2"),sQuery(id+"F0.wireOp",EDGE,"E9.20.0"),sQuery(id+"F0.wireOp",EDGE,"E9.20.1"),sQuery(id+"F0.wireOp",EDGE,"E9.20.2"),sQuery(id+"F0.wireOp",EDGE,"E9.21.0"),sQuery(id+"F0.wireOp",EDGE,"E9.21.1"),sQuery(id+"F0.wireOp",EDGE,"E9.21.2"),sQuery(id+"F0.wireOp",EDGE,"E9.22.0"),sQuery(id+"F0.wireOp",EDGE,"E9.22.1"),sQuery(id+"F0.wireOp",EDGE,"E9.22.2"),sQuery(id+"F0.wireOp",EDGE,"E9.23.0"),sQuery(id+"F0.wireOp",EDGE,"E9.23.1"),sQuery(id+"F0.wireOp",EDGE,"E9.23.2"),sQuery(id+"F0.wireOp",EDGE,"E9.24.0"),sQuery(id+"F0.wireOp",EDGE,"E9.24.1"),sQuery(id+"F0.wireOp",EDGE,"E9.24.2"),sQuery(id+"F0.wireOp",EDGE,"E9.25.0"),sQuery(id+"F0.wireOp",EDGE,"E9.25.1"),sQuery(id+"F0.wireOp",EDGE,"E9.25.2"),sQuery(id+"F0.wireOp",EDGE,"E9.26.0"),sQuery(id+"F0.wireOp",EDGE,"E9.26.1"),sQuery(id+"F0.wireOp",EDGE,"E9.26.2"),sQuery(id+"F0.wireOp",EDGE,"E9.27.0"),sQuery(id+"F0.wireOp",EDGE,"E9.27.1"),sQuery(id+"F0.wireOp",EDGE,"E9.27.2"),sQuery(id+"F0.wireOp",EDGE,"E9.28.0"),sQuery(id+"F0.wireOp",EDGE,"E9.28.1"),sQuery(id+"F0.wireOp",EDGE,"E9.28.2"),sQuery(id+"F0.wireOp",EDGE,"E9.29.0"),sQuery(id+"F0.wireOp",EDGE,"E9.29.1"),sQuery(id+"F0.wireOp",EDGE,"E9.29.2"),sQuery(id+"F0.wireOp",EDGE,"E9.30.0"),sQuery(id+"F0.wireOp",EDGE,"E9.30.1"),sQuery(id+"F0.wireOp",EDGE,"E9.30.2"),sQuery(id+"F0.wireOp",EDGE,"E9.31.0"),sQuery(id+"F0.wireOp",EDGE,"E9.31.1"),sQuery(id+"F0.wireOp",EDGE,"E9.31.2"),sQuery(id+"F0.wireOp",EDGE,"E9.32.0"),sQuery(id+"F0.wireOp",EDGE,"E9.32.1"),sQuery(id+"F0.wireOp",EDGE,"E9.32.2"),sQuery(id+"F0.wireOp",EDGE,"E9.33.0"),sQuery(id+"F0.wireOp",EDGE,"E9.33.1"),sQuery(id+"F0.wireOp",EDGE,"E9.33.2"),sQuery(id+"F0.wireOp",EDGE,"E9.34.0"),sQuery(id+"F0.wireOp",EDGE,"E9.34.1"),sQuery(id+"F0.wireOp",EDGE,"E9.34.2"),sQuery(id+"F0.wireOp",EDGE,"E9.35.0"),sQuery(id+"F0.wireOp",EDGE,"E9.35.1"),sQuery(id+"F0.wireOp",EDGE,"E9.35.2"),sQuery(id+"F0.wireOp",EDGE,"E9.36.0"),sQuery(id+"F0.wireOp",EDGE,"E9.36.1"),sQuery(id+"F0.wireOp",EDGE,"E9.36.2"),sQuery(id+"F0.wireOp",EDGE,"E9.37.0"),sQuery(id+"F0.wireOp",EDGE,"E9.37.1"),sQuery(id+"F0.wireOp",EDGE,"E9.37.2"),sQuery(id+"F0.wireOp",EDGE,"E9.38.0"),sQuery(id+"F0.wireOp",EDGE,"E9.38.1"),sQuery(id+"F0.wireOp",EDGE,"E9.38.2"),sQuery(id+"F0.wireOp",EDGE,"E9.39.0"),sQuery(id+"F0.wireOp",EDGE,"E9.39.1"),sQuery(id+"F0.wireOp",EDGE,"E9.39.2"),sQuery(id+"F0.wireOp",EDGE,"E9.40.0"),sQuery(id+"F0.wireOp",EDGE,"E9.40.1"),sQuery(id+"F0.wireOp",EDGE,"E9.40.2"),sQuery(id+"F0.wireOp",EDGE,"E9.41.0"),sQuery(id+"F0.wireOp",EDGE,"E9.41.1"),sQuery(id+"F0.wireOp",EDGE,"E9.41.2"),sQuery(id+"F0.wireOp",EDGE,"E9.42.0"),sQuery(id+"F0.wireOp",EDGE,"E9.42.1"),sQuery(id+"F0.wireOp",EDGE,"E9.42.2"),sQuery(id+"F0.wireOp",EDGE,"E9.43.0"),sQuery(id+"F0.wireOp",EDGE,"E9.43.1"),sQuery(id+"F0.wireOp",EDGE,"E9.43.2"),sQuery(id+"F0.wireOp",EDGE,"E9.44.0"),sQuery(id+"F0.wireOp",EDGE,"E9.44.1"),sQuery(id+"F0.wireOp",EDGE,"E9.44.2"),sQuery(id+"F0.wireOp",EDGE,"E9.45.0"),sQuery(id+"F0.wireOp",EDGE,"E9.45.1"),sQuery(id+"F0.wireOp",EDGE,"E9.45.2"),sQuery(id+"F0.wireOp",EDGE,"E9.46.0"),sQuery(id+"F0.wireOp",EDGE,"E9.46.1"),sQuery(id+"F0.wireOp",EDGE,"E9.46.2"),sQuery(id+"F0.wireOp",EDGE,"E9.47.0"),sQuery(id+"F0.wireOp",EDGE,"E9.47.1"),sQuery(id+"F0.wireOp",EDGE,"E9.47.2"),sQuery(id+"F0.wireOp",EDGE,"E9.48.0"),sQuery(id+"F0.wireOp",EDGE,"E9.48.1"),sQuery(id+"F0.wireOp",EDGE,"E9.48.2"),sQuery(id+"F0.wireOp",EDGE,"E9.49.0"),sQuery(id+"F0.wireOp",EDGE,"E9.49.1"),sQuery(id+"F0.wireOp",EDGE,"E9.49.2"),sQuery(id+"F0.wireOp",EDGE,"E9.50.0"),sQuery(id+"F0.wireOp",EDGE,"E9.50.1"),sQuery(id+"F0.wireOp",EDGE,"E9.50.2"),sQuery(id+"F0.wireOp",EDGE,"E9.51.0"),sQuery(id+"F0.wireOp",EDGE,"E9.51.1"),sQuery(id+"F0.wireOp",EDGE,"E9.51.2"),sQuery(id+"F0.wireOp",EDGE,"E9.52.0"),sQuery(id+"F0.wireOp",EDGE,"E9.52.1"),sQuery(id+"F0.wireOp",EDGE,"E9.52.2"),sQuery(id+"F0.wireOp",EDGE,"E9.53.0"),sQuery(id+"F0.wireOp",EDGE,"E9.53.1"),sQuery(id+"F0.wireOp",EDGE,"E9.53.2"),sQuery(id+"F0.wireOp",EDGE,"E9.54.0"),sQuery(id+"F0.wireOp",EDGE,"E9.54.1"),sQuery(id+"F0.wireOp",EDGE,"E9.54.2"),sQuery(id+"F0.wireOp",EDGE,"E9.55.0"),sQuery(id+"F0.wireOp",EDGE,"E9.55.1"),sQuery(id+"F0.wireOp",EDGE,"E9.55.2"),sQuery(id+"F0.wireOp",EDGE,"E9.56.0"),sQuery(id+"F0.wireOp",EDGE,"E9.56.1"),sQuery(id+"F0.wireOp",EDGE,"E9.56.2"),sQuery(id+"F0.wireOp",EDGE,"E9.57.0"),sQuery(id+"F0.wireOp",EDGE,"E9.57.1"),sQuery(id+"F0.wireOp",EDGE,"E9.57.2"),sQuery(id+"F0.wireOp",EDGE,"E9.58.0"),sQuery(id+"F0.wireOp",EDGE,"E9.58.1"),sQuery(id+"F0.wireOp",EDGE,"E9.58.2"),sQuery(id+"F0.wireOp",EDGE,"E9.59.0"),sQuery(id+"F0.wireOp",EDGE,"E9.59.1"),sQuery(id+"F0.wireOp",EDGE,"E9.59.2"),sQuery(id+"F0.wireOp",EDGE,"E9.60.0"),sQuery(id+"F0.wireOp",EDGE,"E9.60.1"),sQuery(id+"F0.wireOp",EDGE,"E9.60.2"),sQuery(id+"F0.wireOp",EDGE,"E9.61.0"),sQuery(id+"F0.wireOp",EDGE,"E9.61.1"),sQuery(id+"F0.wireOp",EDGE,"E9.61.2"),sQuery(id+"F0.wireOp",EDGE,"E9.62.0"),sQuery(id+"F0.wireOp",EDGE,"E9.62.1"),sQuery(id+"F0.wireOp",EDGE,"E9.62.2"),sQuery(id+"F0.wireOp",EDGE,"E9.63.0"),sQuery(id+"F0.wireOp",EDGE,"E9.63.1"),sQuery(id+"F0.wireOp",EDGE,"E9.63.2"),sQuery(id+"F0.wireOp",EDGE,"E9.64.0"),sQuery(id+"F0.wireOp",EDGE,"E9.64.1"),sQuery(id+"F0.wireOp",EDGE,"E9.64.2"),sQuery(id+"F0.wireOp",EDGE,"E9.65.0"),sQuery(id+"F0.wireOp",EDGE,"E9.65.1"),sQuery(id+"F0.wireOp",EDGE,"E9.65.2"),sQuery(id+"F0.wireOp",EDGE,"E9.66.0"),sQuery(id+"F0.wireOp",EDGE,"E9.66.1"),sQuery(id+"F0.wireOp",EDGE,"E9.66.2"),sQuery(id+"F0.wireOp",EDGE,"E9.67.0"),sQuery(id+"F0.wireOp",EDGE,"E9.67.1"),sQuery(id+"F0.wireOp",EDGE,"E9.67.2"),sQuery(id+"F0.wireOp",EDGE,"E9.68.0"),sQuery(id+"F0.wireOp",EDGE,"E9.68.1"),sQuery(id+"F0.wireOp",EDGE,"E9.68.2"),sQuery(id+"F0.wireOp",EDGE,"E9.69.0"),sQuery(id+"F0.wireOp",EDGE,"E9.69.1"),sQuery(id+"F0.wireOp",EDGE,"E9.69.2"),sQuery(id+"F0.wireOp",EDGE,"E9.70.0"),sQuery(id+"F0.wireOp",EDGE,"E9.70.1"),sQuery(id+"F0.wireOp",EDGE,"E9.70.2"),sQuery(id+"F0.wireOp",EDGE,"E9.71.0"),sQuery(id+"F0.wireOp",EDGE,"E9.71.1"),sQuery(id+"F0.wireOp",EDGE,"E9.71.2"),sQuery(id+"F0.wireOp",EDGE,"E9.72.0"),sQuery(id+"F0.wireOp",EDGE,"E9.72.1"),sQuery(id+"F0.wireOp",EDGE,"E9.72.2"),sQuery(id+"F0.wireOp",EDGE,"E9.73.0"),sQuery(id+"F0.wireOp",EDGE,"E9.73.1"),sQuery(id+"F0.wireOp",EDGE,"E9.73.2"),sQuery(id+"F0.wireOp",EDGE,"E9.74.0"),sQuery(id+"F0.wireOp",EDGE,"E9.74.1"),sQuery(id+"F0.wireOp",EDGE,"E9.74.2"),sQuery(id+"F0.wireOp",EDGE,"E9.75.0"),sQuery(id+"F0.wireOp",EDGE,"E9.75.1"),sQuery(id+"F0.wireOp",EDGE,"E9.75.2"),sQuery(id+"F0.wireOp",EDGE,"E9.76.0"),sQuery(id+"F0.wireOp",EDGE,"E9.76.1"),sQuery(id+"F0.wireOp",EDGE,"E9.76.2"),sQuery(id+"F0.wireOp",EDGE,"E9.77.0"),sQuery(id+"F0.wireOp",EDGE,"E9.77.1"),sQuery(id+"F0.wireOp",EDGE,"E9.77.2"),sQuery(id+"F0.wireOp",EDGE,"E9.78.0"),sQuery(id+"F0.wireOp",EDGE,"E9.78.1"),sQuery(id+"F0.wireOp",EDGE,"E9.78.2"),sQuery(id+"F0.wireOp",EDGE,"E9.79.0"),sQuery(id+"F0.wireOp",EDGE,"E9.79.1"),sQuery(id+"F0.wireOp",EDGE,"E9.79.2")])],"isStart":false});
            var sketch = newSketch(context, id + "F10", { "sketchPlane" : qUnion([Q0])});
            skCircle(sketch, "E55.0", {"center": v(0, 66) * mm, "radius": 4 * mm});
            skCircle(sketch, "E56.0", {"center": v(-57.16, 33) * mm, "radius": 4 * mm});
            skCircle(sketch, "E57.0", {"center": v(-57.16, -33) * mm, "radius": 4 * mm});
            skCircle(sketch, "E58.0", {"center": v(0, -66) * mm, "radius": 4 * mm});
            skCircle(sketch, "E59.0", {"center": v(57.16, -33) * mm, "radius": 4 * mm});
            skCircle(sketch, "E60.0", {"center": v(57.16, 33) * mm, "radius": 4 * mm});
            skSolve(sketch);
        }
        {
            var Q0;
            Q0=qSketchRegion(id+"F10",true);
            extrude(context, id + "F11", {"entities" : qUnion([Q0]), "operationType" : NewBodyOperationType.REMOVE, "oppositeDirection" : true, "depth" : 5 * mm, "offsetDistance" : 25 * mm});
        }
    });
